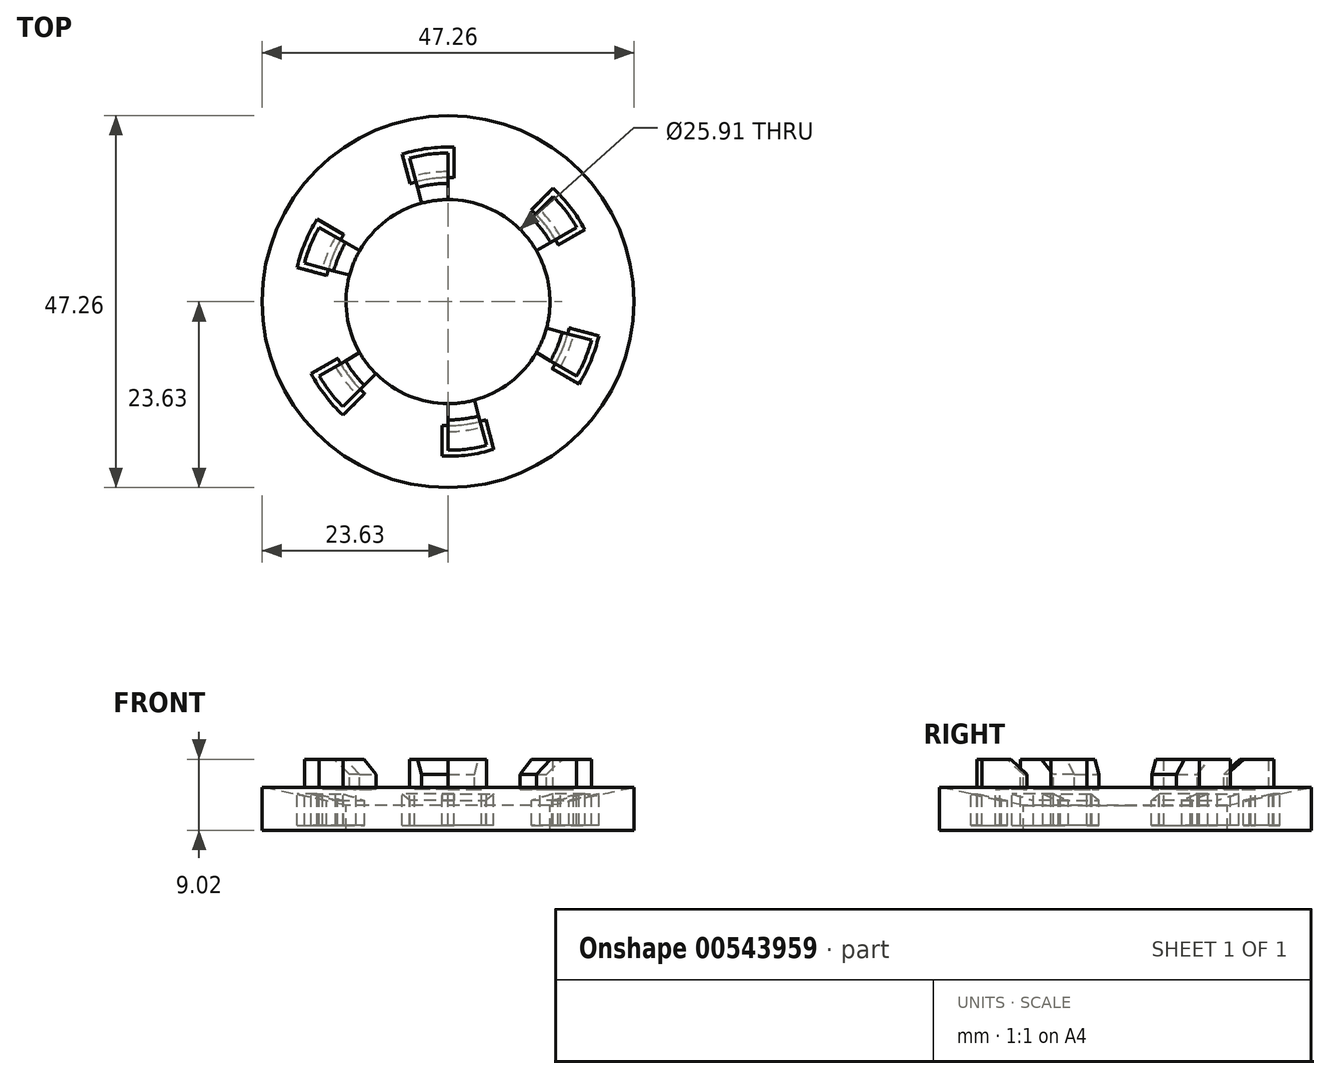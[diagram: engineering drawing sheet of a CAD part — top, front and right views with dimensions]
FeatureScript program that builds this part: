
annotation { "Feature Type Name" : "Feature", "Feature Type Description" : "" }
export const myFeature = defineFeature(function(context is Context, id is Id, definition is map)
    precondition{}
    {
        {
            var Q0;
            Q0=qCreatedBy(makeId("Front.planeOp"),FACE);
            var sketch = newSketch(context, id + "F0", { "sketchPlane" : qUnion([Q0])});
            skLineSegment(sketch, "E0", {"start": v(0, 0) * mm, "end": v(16.51, 0) * mm});
            skLineSegment(sketch, "E1", {"start": v(16.51, -1.27) * mm, "end": v(16.51, 0) * mm});
            skLineSegment(sketch, "E2", {"start": v(0, -2.03) * mm, "end": v(12.95, -2.03) * mm});
            skLineSegment(sketch, "E3", {"start": v(12.95, -2.03) * mm, "end": v(16.51, -1.27) * mm});
            skLineSegment(sketch, "E4", {"start": v(12.95, 0) * mm, "end": v(12.95, 3.81) * mm});
            skLineSegment(sketch, "E5", {"start": v(12.95, 3.81) * mm, "end": v(23.63, 3.81) * mm});
            skLineSegment(sketch, "E6", {"start": v(23.63, 3.81) * mm, "end": v(23.63, -5.2) * mm});
            skLineSegment(sketch, "E7", {"start": v(23.63, -5.2) * mm, "end": v(12.95, -5.2) * mm});
            skLineSegment(sketch, "E8", {"start": v(12.95, -5.2) * mm, "end": v(12.95, -2.03) * mm});
            skLineSegment(sketch, "E9", {"start": v(0, 0) * mm, "end": v(0, -2.03) * mm});
            skLineSegment(sketch, "E10", {"start": v(12.95, 1.9) * mm, "end": v(15.03, 3.81) * mm});
            skSolve(sketch);
        }
        {
            var Q0;
            {var subQ4=sQuery(id+"F0.wireOp",EDGE,"E1");Q0=makeQuery(id+"F0.imprint","IMPRINT",FACE,{"disambiguationData":[TD([[makeQuery(id+"F0.imprint","IMPRINT",EDGE,{"derivedFrom":subQ4}),-1.0]])]});}
            var Q1;
            Q1=sQuery(id+"F0.wireOp",EDGE,"E9");
            revolve(context, id + "F1", {"entities" : qUnion([Q0]), "axis" : qUnion([Q1]), "revolveType" : RevolveType.FULL});
        }
        {
            var Q0;
            Q0=makeQuery(id+"F1.opRevolve","SWEPT_FACE",FACE,{"disambiguationData":[OSD([sQuery(id+"F0.wireOp",EDGE,"E5")])]});
            var sketch = newSketch(context, id + "F2", { "sketchPlane" : qUnion([Q0])});
            skLineSegment(sketch, "E11", {"start": v(0, 0) * mm, "end": v(16.7, 16.7) * mm});
            skLineSegment(sketch, "E12", {"start": v(0, 0) * mm, "end": v(0, 23.63) * mm});
            skArc(sketch, "E13.0", {"start": v(16.7, 16.7) * mm, "mid": v(9.04, 21.83) * mm, "end": v(0, 23.63) * mm});
            skLineSegment(sketch, "E14.1.0", {"start": v(0, 0) * mm, "end": v(-20.46, 11.82) * mm});
            skLineSegment(sketch, "E14.1.1", {"start": v(0, 0) * mm, "end": v(-6.12, 22.83) * mm});
            skArc(sketch, "E14.1.2", {"start": v(-6.12, 22.83) * mm, "mid": v(-14.39, 18.75) * mm, "end": v(-20.46, 11.82) * mm});
            skLineSegment(sketch, "E14.2.0", {"start": v(0, 0) * mm, "end": v(-20.46, -11.82) * mm});
            skLineSegment(sketch, "E14.2.1", {"start": v(0, 0) * mm, "end": v(-22.83, 6.12) * mm});
            skArc(sketch, "E14.2.2", {"start": v(-22.83, 6.12) * mm, "mid": v(-23.43, -3.08) * mm, "end": v(-20.46, -11.82) * mm});
            skLineSegment(sketch, "E15.2.3.0", {"start": v(0, 0) * mm, "end": v(0, -23.63) * mm});
            skLineSegment(sketch, "E15.3.3.0", {"start": v(0, 0) * mm, "end": v(-16.7, -16.7) * mm});
            skArc(sketch, "E15.6.3.0", {"start": v(-16.7, -16.7) * mm, "mid": v(-9.04, -21.83) * mm, "end": v(0, -23.63) * mm});
            skLineSegment(sketch, "E16.2.4.0", {"start": v(0, 0) * mm, "end": v(20.46, -11.82) * mm});
            skLineSegment(sketch, "E16.3.4.0", {"start": v(0, 0) * mm, "end": v(6.12, -22.83) * mm});
            skArc(sketch, "E16.6.4.0", {"start": v(6.12, -22.83) * mm, "mid": v(14.39, -18.75) * mm, "end": v(20.46, -11.82) * mm});
            skLineSegment(sketch, "E17.2.5.0", {"start": v(0, 0) * mm, "end": v(20.46, 11.82) * mm});
            skLineSegment(sketch, "E17.3.5.0", {"start": v(0, 0) * mm, "end": v(22.83, -6.12) * mm});
            skArc(sketch, "E17.6.5.0", {"start": v(22.83, -6.12) * mm, "mid": v(23.43, 3.08) * mm, "end": v(20.46, 11.82) * mm});
            skSolve(sketch);
        }
        {
            var Q0;
            Q0 = qSketchRegion(id + "F2", true);
            var Q1;
            Q1=makeQuery(id+"F1.opRevolve","SWEPT_FACE",FACE,{"disambiguationData":[OSD([sQuery(id+"F0.wireOp",EDGE,"E3")])]});
            extrude(context, id + "F3", {"entities" : qUnion([Q0]), "operationType" : NewBodyOperationType.REMOVE, "endBound" : BoundingType.UP_TO_SURFACE, "oppositeDirection" : true, "depth" : 25.4 * mm, "endBoundEntityFace" : qUnion([Q1]), "offsetDistance" : 25.4 * mm});
        }
        {
            var Q0;
            Q0=makeQuery(id+"F3.boolean.opBoolean","SPLIT",FACE,{"disambiguationData":[TD([makeQuery(id+"F3.opExtrude","SWEPT_FACE",FACE,{"disambiguationData":[OSD([sQuery(id+"F2.wireOp",EDGE,"E14.2.0")])]})])],"derivedFrom":makeQuery(id+"F1.opRevolve","SWEPT_FACE",FACE,{"disambiguationData":[OSD([sQuery(id+"F0.wireOp",EDGE,"E5")])]})});
            var sketch = newSketch(context, id + "F4", { "sketchPlane" : qUnion([Q0])});
            skCircle(sketch, "E18", {"center": v(0, 0) * mm, "radius": 18.88 * mm});
            skCircle(sketch, "E19", {"center": v(0, 0) * mm, "radius": 25.99 * mm});
            skSolve(sketch);
        }
        {
            var Q0;
            Q0 = qSketchRegion(id + "F4", true);
            var Q1;
            Q1=makeQuery(id+"F3.boolean.opBoolean","MERGE",FACE,{"derivedFrom":[makeQuery(id+"F1.opRevolve","SWEPT_FACE",FACE,{"disambiguationData":[OSD([sQuery(id+"F0.wireOp",EDGE,"E3")])]})],"fromTools":[makeQuery(id+"F3.opExtrude","CAP_FACE",FACE,{"disambiguationData":[OSD([sQuery(id+"F2.wireOp",EDGE,"E11"),sQuery(id+"F2.wireOp",EDGE,"E12"),sQuery(id+"F2.wireOp",EDGE,"E13.0")])],"isStart":false}),makeQuery(id+"F3.opExtrude","CAP_FACE",FACE,{"disambiguationData":[OSD([sQuery(id+"F2.wireOp",EDGE,"E14.1.0"),sQuery(id+"F2.wireOp",EDGE,"E14.1.1"),sQuery(id+"F2.wireOp",EDGE,"E14.1.2")])],"isStart":false}),makeQuery(id+"F3.opExtrude","CAP_FACE",FACE,{"disambiguationData":[OSD([sQuery(id+"F2.wireOp",EDGE,"E14.2.0"),sQuery(id+"F2.wireOp",EDGE,"E14.2.1"),sQuery(id+"F2.wireOp",EDGE,"E14.2.2")])],"isStart":false}),makeQuery(id+"F3.opExtrude","CAP_FACE",FACE,{"disambiguationData":[OSD([sQuery(id+"F2.wireOp",EDGE,"E15.2.3.0"),sQuery(id+"F2.wireOp",EDGE,"E15.3.3.0"),sQuery(id+"F2.wireOp",EDGE,"E15.6.3.0")])],"isStart":false}),makeQuery(id+"F3.opExtrude","CAP_FACE",FACE,{"disambiguationData":[OSD([sQuery(id+"F2.wireOp",EDGE,"E16.2.4.0"),sQuery(id+"F2.wireOp",EDGE,"E16.3.4.0"),sQuery(id+"F2.wireOp",EDGE,"E16.6.4.0")])],"isStart":false}),makeQuery(id+"F3.opExtrude","CAP_FACE",FACE,{"disambiguationData":[OSD([sQuery(id+"F2.wireOp",EDGE,"E17.2.5.0"),sQuery(id+"F2.wireOp",EDGE,"E17.3.5.0"),sQuery(id+"F2.wireOp",EDGE,"E17.6.5.0")])],"isStart":false})]});
            extrude(context, id + "F5", {"entities" : qUnion([Q0]), "operationType" : NewBodyOperationType.REMOVE, "endBound" : BoundingType.UP_TO_SURFACE, "oppositeDirection" : true, "depth" : 25.4 * mm, "endBoundEntityFace" : qUnion([Q1]), "offsetDistance" : 25.4 * mm});
        }
        {
            var Q0;
            Q0=makeQuery(id+"F3.boolean.opBoolean","SPLIT",FACE,{"disambiguationData":[TD([makeQuery(id+"F3.opExtrude","SWEPT_FACE",FACE,{"disambiguationData":[OSD([sQuery(id+"F2.wireOp",EDGE,"E11")])]})])],"derivedFrom":makeQuery(id+"F1.opRevolve","SWEPT_FACE",FACE,{"disambiguationData":[OSD([sQuery(id+"F0.wireOp",EDGE,"E0")])]})});
            var sketch = newSketch(context, id + "F6", { "sketchPlane" : qUnion([Q0])});
            skLineSegment(sketch, "E20.0", {"start": v(13.35, -13.35) * mm, "end": v(11.67, -11.67) * mm});
            skArc(sketch, "E21.0", {"start": v(14.3, -8.26) * mm, "mid": v(13.1, -10.05) * mm, "end": v(11.67, -11.67) * mm});
            skArc(sketch, "E22.0", {"start": v(13.35, -13.35) * mm, "mid": v(14.98, -11.5) * mm, "end": v(16.35, -9.44) * mm});
            skArc(sketch, "E23.0", {"start": v(14, -7.2) * mm, "mid": v(12.5, -9.59) * mm, "end": v(10.58, -11.66) * mm});
            skLineSegment(sketch, "E24.0", {"start": v(13.34, -14.42) * mm, "end": v(10.58, -11.66) * mm});
            skArc(sketch, "E25.0", {"start": v(13.34, -14.42) * mm, "mid": v(15.58, -11.96) * mm, "end": v(17.38, -9.15) * mm});
            skLineSegment(sketch, "E26.0", {"start": v(16.35, -9.44) * mm, "end": v(14.3, -8.26) * mm});
            skLineSegment(sketch, "E27.0", {"start": v(17.38, -9.15) * mm, "end": v(14, -7.2) * mm});
            skLineSegment(sketch, "E28.1.0", {"start": v(19.15, 4.34) * mm, "end": v(15.4, 3.34) * mm});
            skArc(sketch, "E28.1.1", {"start": v(18.24, 4.89) * mm, "mid": v(17.44, 7.22) * mm, "end": v(16.35, 9.44) * mm});
            skArc(sketch, "E28.1.2", {"start": v(14.3, 8.25) * mm, "mid": v(15.25, 6.32) * mm, "end": v(15.95, 4.27) * mm});
            skArc(sketch, "E28.1.3", {"start": v(19.15, 4.34) * mm, "mid": v(18.15, 7.52) * mm, "end": v(16.62, 10.47) * mm});
            skLineSegment(sketch, "E28.1.4", {"start": v(16.62, 10.47) * mm, "end": v(13.24, 8.52) * mm});
            skArc(sketch, "E28.1.5", {"start": v(13.24, 8.52) * mm, "mid": v(14.55, 6.03) * mm, "end": v(15.4, 3.34) * mm});
            skLineSegment(sketch, "E28.1.6", {"start": v(16.35, 9.44) * mm, "end": v(14.3, 8.25) * mm});
            skLineSegment(sketch, "E28.1.7", {"start": v(18.24, 4.89) * mm, "end": v(15.95, 4.27) * mm});
            skLineSegment(sketch, "E28.2.0", {"start": v(5.82, 18.76) * mm, "end": v(4.8, 15) * mm});
            skArc(sketch, "E28.2.1", {"start": v(4.89, 18.24) * mm, "mid": v(2.46, 18.72) * mm, "end": v(0, 18.88) * mm});
            skArc(sketch, "E28.2.2", {"start": v(0, 16.51) * mm, "mid": v(2.15, 16.37) * mm, "end": v(4.27, 15.95) * mm});
            skArc(sketch, "E28.2.3", {"start": v(5.82, 18.76) * mm, "mid": v(2.56, 19.47) * mm, "end": v(-0.76, 19.63) * mm});
            skLineSegment(sketch, "E28.2.4", {"start": v(-0.76, 19.63) * mm, "end": v(-0.76, 15.73) * mm});
            skArc(sketch, "E28.2.5", {"start": v(-0.76, 15.73) * mm, "mid": v(2.06, 15.61) * mm, "end": v(4.8, 15) * mm});
            skLineSegment(sketch, "E28.2.6", {"start": v(0, 18.88) * mm, "end": v(0, 16.51) * mm});
            skLineSegment(sketch, "E28.2.7", {"start": v(4.89, 18.24) * mm, "end": v(4.27, 15.95) * mm});
            skLineSegment(sketch, "E28.3.0", {"start": v(-13.34, 14.42) * mm, "end": v(-10.58, 11.66) * mm});
            skArc(sketch, "E28.3.1", {"start": v(-13.35, 13.35) * mm, "mid": v(-14.98, 11.5) * mm, "end": v(-16.35, 9.44) * mm});
            skArc(sketch, "E28.3.2", {"start": v(-14.3, 8.26) * mm, "mid": v(-13.1, 10.05) * mm, "end": v(-11.67, 11.67) * mm});
            skArc(sketch, "E28.3.3", {"start": v(-13.34, 14.42) * mm, "mid": v(-15.58, 11.96) * mm, "end": v(-17.38, 9.15) * mm});
            skLineSegment(sketch, "E28.3.4", {"start": v(-17.38, 9.15) * mm, "end": v(-14, 7.2) * mm});
            skArc(sketch, "E28.3.5", {"start": v(-14, 7.2) * mm, "mid": v(-12.5, 9.59) * mm, "end": v(-10.58, 11.66) * mm});
            skLineSegment(sketch, "E28.3.6", {"start": v(-16.35, 9.44) * mm, "end": v(-14.3, 8.26) * mm});
            skLineSegment(sketch, "E28.3.7", {"start": v(-13.35, 13.35) * mm, "end": v(-11.67, 11.67) * mm});
            skLineSegment(sketch, "E28.4.0", {"start": v(-19.15, -4.34) * mm, "end": v(-15.4, -3.34) * mm});
            skArc(sketch, "E28.4.1", {"start": v(-18.24, -4.89) * mm, "mid": v(-17.44, -7.22) * mm, "end": v(-16.35, -9.44) * mm});
            skArc(sketch, "E28.4.2", {"start": v(-14.3, -8.25) * mm, "mid": v(-15.25, -6.32) * mm, "end": v(-15.95, -4.27) * mm});
            skArc(sketch, "E28.4.3", {"start": v(-19.15, -4.34) * mm, "mid": v(-18.15, -7.52) * mm, "end": v(-16.62, -10.47) * mm});
            skLineSegment(sketch, "E28.4.4", {"start": v(-16.62, -10.47) * mm, "end": v(-13.24, -8.52) * mm});
            skArc(sketch, "E28.4.5", {"start": v(-13.24, -8.52) * mm, "mid": v(-14.55, -6.03) * mm, "end": v(-15.4, -3.34) * mm});
            skLineSegment(sketch, "E28.4.6", {"start": v(-16.35, -9.44) * mm, "end": v(-14.3, -8.25) * mm});
            skLineSegment(sketch, "E28.4.7", {"start": v(-18.24, -4.89) * mm, "end": v(-15.95, -4.27) * mm});
            skLineSegment(sketch, "E28.5.0", {"start": v(-5.82, -18.76) * mm, "end": v(-4.8, -15) * mm});
            skArc(sketch, "E28.5.1", {"start": v(-4.89, -18.24) * mm, "mid": v(-2.46, -18.72) * mm, "end": v(0, -18.88) * mm});
            skArc(sketch, "E28.5.2", {"start": v(0, -16.51) * mm, "mid": v(-2.15, -16.37) * mm, "end": v(-4.27, -15.95) * mm});
            skArc(sketch, "E28.5.3", {"start": v(-5.82, -18.76) * mm, "mid": v(-2.56, -19.47) * mm, "end": v(0.76, -19.63) * mm});
            skLineSegment(sketch, "E28.5.4", {"start": v(0.76, -19.63) * mm, "end": v(0.76, -15.73) * mm});
            skArc(sketch, "E28.5.5", {"start": v(0.76, -15.73) * mm, "mid": v(-2.06, -15.61) * mm, "end": v(-4.8, -15) * mm});
            skLineSegment(sketch, "E28.5.6", {"start": v(0, -18.88) * mm, "end": v(0, -16.51) * mm});
            skLineSegment(sketch, "E28.5.7", {"start": v(-4.89, -18.24) * mm, "end": v(-4.27, -15.95) * mm});
            skSolve(sketch);
        }
        {
            var Q0;
            Q0 = qSketchRegion(id + "F6", true);
            extrude(context, id + "F7", {"entities" : qUnion([Q0]), "operationType" : NewBodyOperationType.REMOVE, "depth" : 4.57 * mm, "offsetDistance" : 25.4 * mm});
        }
    });
